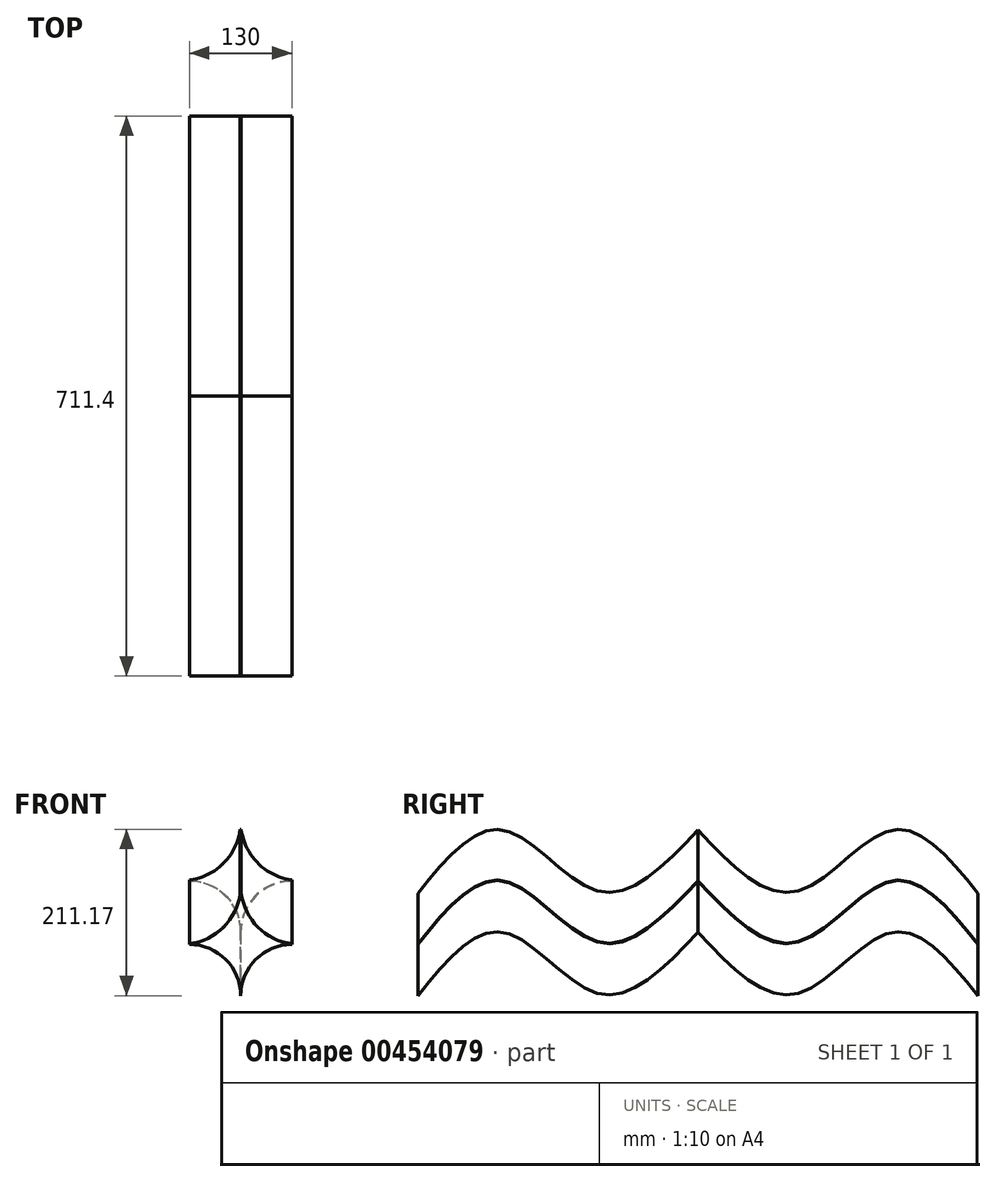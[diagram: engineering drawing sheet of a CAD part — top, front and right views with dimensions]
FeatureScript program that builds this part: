
annotation { "Feature Type Name" : "Feature", "Feature Type Description" : "" }
export const myFeature = defineFeature(function(context is Context, id is Id, definition is map)
    precondition{}
    {
        {
            var Q0;
            Q0=qCreatedBy(makeId("Front.planeOp"),FACE);
            var sketch = newSketch(context, id + "F0", { "sketchPlane" : qUnion([Q0])});
            skLineSegment(sketch, "E0.bottom", {"start": v(-75, 75) * mm, "end": v(75, 75) * mm});
            skLineSegment(sketch, "E0.top", {"start": v(-75, -75) * mm, "end": v(75, -75) * mm});
            skLineSegment(sketch, "E0.left", {"start": v(-75, 75) * mm, "end": v(-75, -75) * mm});
            skLineSegment(sketch, "E0.right", {"start": v(75, 75) * mm, "end": v(75, -75) * mm});
            skPoint(sketch, "E0.middle", {"position": v(0, 0) * mm});
            skPoint(sketch, "E1", {"position": v(0, 75) * mm});
            skPoint(sketch, "E2", {"position": v(75, 0) * mm});
            skPoint(sketch, "E3", {"position": v(-75, 0) * mm});
            skPoint(sketch, "E4", {"position": v(0, -75) * mm});
            skArc(sketch, "E5", {"start": v(0, 75) * mm, "mid": v(21.97, 21.97) * mm, "end": v(75, 0) * mm});
            skArc(sketch, "E6", {"start": v(-75, 0) * mm, "mid": v(-21.97, 21.97) * mm, "end": v(0, 75) * mm});
            skArc(sketch, "E7", {"start": v(-75, 0) * mm, "mid": v(-21.97, -21.97) * mm, "end": v(0, -75) * mm});
            skArc(sketch, "E8", {"start": v(75, 0) * mm, "mid": v(21.97, -21.97) * mm, "end": v(0, -75) * mm});
            skArc(sketch, "E9.MirrorCS", {"start": v(0, 75) * mm, "mid": v(-21.97, 21.97) * mm, "end": v(-75, 0) * mm});
            skLineSegment(sketch, "E10.MirrorCS", {"start": v(75, 75) * mm, "end": v(-75, 75) * mm});
            skLineSegment(sketch, "E11.0", {"start": v(65, 65) * mm, "end": v(-65, 65) * mm});
            skLineSegment(sketch, "E11.1", {"start": v(65, 65) * mm, "end": v(65, -65) * mm});
            skLineSegment(sketch, "E11.2", {"start": v(-65, -65) * mm, "end": v(65, -65) * mm});
            skLineSegment(sketch, "E11.3", {"start": v(-65, 65) * mm, "end": v(-65, -65) * mm});
            skPoint(sketch, "E12", {"position": v(-65, 0) * mm});
            skPoint(sketch, "E13", {"position": v(0, 65) * mm});
            skPoint(sketch, "E14", {"position": v(65, 0) * mm});
            skPoint(sketch, "E15", {"position": v(0, -65) * mm});
            skArc(sketch, "E16", {"start": v(-65, 0) * mm, "mid": v(-19.04, 19.04) * mm, "end": v(0, 65) * mm});
            skArc(sketch, "E17", {"start": v(-65, 0) * mm, "mid": v(-19.04, -19.04) * mm, "end": v(0, -65) * mm});
            skArc(sketch, "E18", {"start": v(0, -65) * mm, "mid": v(19.04, -19.04) * mm, "end": v(65, 0) * mm});
            skArc(sketch, "E19", {"start": v(0, 65) * mm, "mid": v(19.04, 19.04) * mm, "end": v(65, 0) * mm});
            skSolve(sketch);
        }
        {
            var Q0;
            Q0=qCreatedBy(makeId("Right.planeOp"),FACE);
            var sketch = newSketch(context, id + "F1", { "sketchPlane" : qUnion([Q0])});
            skFitSpline(sketch, "E20", {"points": [v(0, 0) * mm, v(124.52, -78.15) * mm, v(247.28, 0) * mm, v(355.7, -80.44) * mm], "startDerivative": vector(366.55, -387.34) * mm, "endDerivative": vector(326.42, -403.83) * mm});
            skSolve(sketch);
        }
        {
            var Q0;
            {var subQ5=sQuery(id+"F0.wireOp",EDGE,"E19");Q0=makeQuery(id+"F0.imprint","IMPRINT",FACE,{"disambiguationData":[TD([[makeQuery(id+"F0.imprint","IMPRINT",EDGE,{"derivedFrom":subQ5}),1.0]])]});}
            var Q1;
            {var subQ5=sQuery(id+"F0.wireOp",EDGE,"E16");Q1=makeQuery(id+"F0.imprint","IMPRINT",FACE,{"disambiguationData":[TD([[makeQuery(id+"F0.imprint","IMPRINT",EDGE,{"derivedFrom":subQ5}),1.0]])]});}
            var Q2;
            {var subQ5=sQuery(id+"F0.wireOp",EDGE,"E17");Q2=makeQuery(id+"F0.imprint","IMPRINT",FACE,{"disambiguationData":[TD([[makeQuery(id+"F0.imprint","IMPRINT",EDGE,{"derivedFrom":subQ5}),-1.0]])]});}
            var Q3;
            {var subQ5=sQuery(id+"F0.wireOp",EDGE,"E18");Q3=makeQuery(id+"F0.imprint","IMPRINT",FACE,{"disambiguationData":[TD([[makeQuery(id+"F0.imprint","IMPRINT",EDGE,{"derivedFrom":subQ5}),-1.0]])]});}
            var Q4;
            Q4=sQuery(id+"F1.wireOp",EDGE,"E20");
            sweep(context, id + "F2", {"profiles" : qUnion([Q0, Q1, Q2, Q3]), "path" : qUnion([Q4]), "keepProfileOrientation" : true});
        }
        {
            var Q0;
            Q0=makeQuery(id+"F2.opSweep","SWEPT_BODY",BODY,{"disambiguationData":[OSD([sQuery(id+"F0.wireOp",EDGE,"E7"),sQuery(id+"F0.wireOp",EDGE,"E11.2"),sQuery(id+"F0.wireOp",EDGE,"E11.3"),sQuery(id+"F0.wireOp",EDGE,"E17"),sQuery(id+"F1.wireOp",EDGE,"E20")])]});
            var Q1;
            Q1=makeQuery(id+"F2.opSweep","SWEPT_BODY",BODY,{"disambiguationData":[OSD([sQuery(id+"F0.wireOp",EDGE,"E9.MirrorCS"),sQuery(id+"F0.wireOp",EDGE,"E11.0"),sQuery(id+"F0.wireOp",EDGE,"E11.3"),sQuery(id+"F0.wireOp",EDGE,"E16"),sQuery(id+"F1.wireOp",EDGE,"E20")])]});
            var Q2;
            Q2=makeQuery(id+"F2.opSweep","SWEPT_BODY",BODY,{"disambiguationData":[OSD([sQuery(id+"F0.wireOp",EDGE,"E5"),sQuery(id+"F0.wireOp",EDGE,"E11.0"),sQuery(id+"F0.wireOp",EDGE,"E11.1"),sQuery(id+"F0.wireOp",EDGE,"E19"),sQuery(id+"F1.wireOp",EDGE,"E20")])]});
            var Q3;
            Q3=makeQuery(id+"F2.opSweep","SWEPT_BODY",BODY,{"disambiguationData":[OSD([sQuery(id+"F0.wireOp",EDGE,"E8"),sQuery(id+"F0.wireOp",EDGE,"E11.1"),sQuery(id+"F0.wireOp",EDGE,"E11.2"),sQuery(id+"F0.wireOp",EDGE,"E18"),sQuery(id+"F1.wireOp",EDGE,"E20")])]});
            var Q4;
            Q4=qCreatedBy(makeId("Front.planeOp"),FACE);
            mirror(context, id + "F3", {"entities" : qUnion([Q0, Q1, Q2, Q3]), "mirrorPlane" : qUnion([Q4])});
        }
    });
